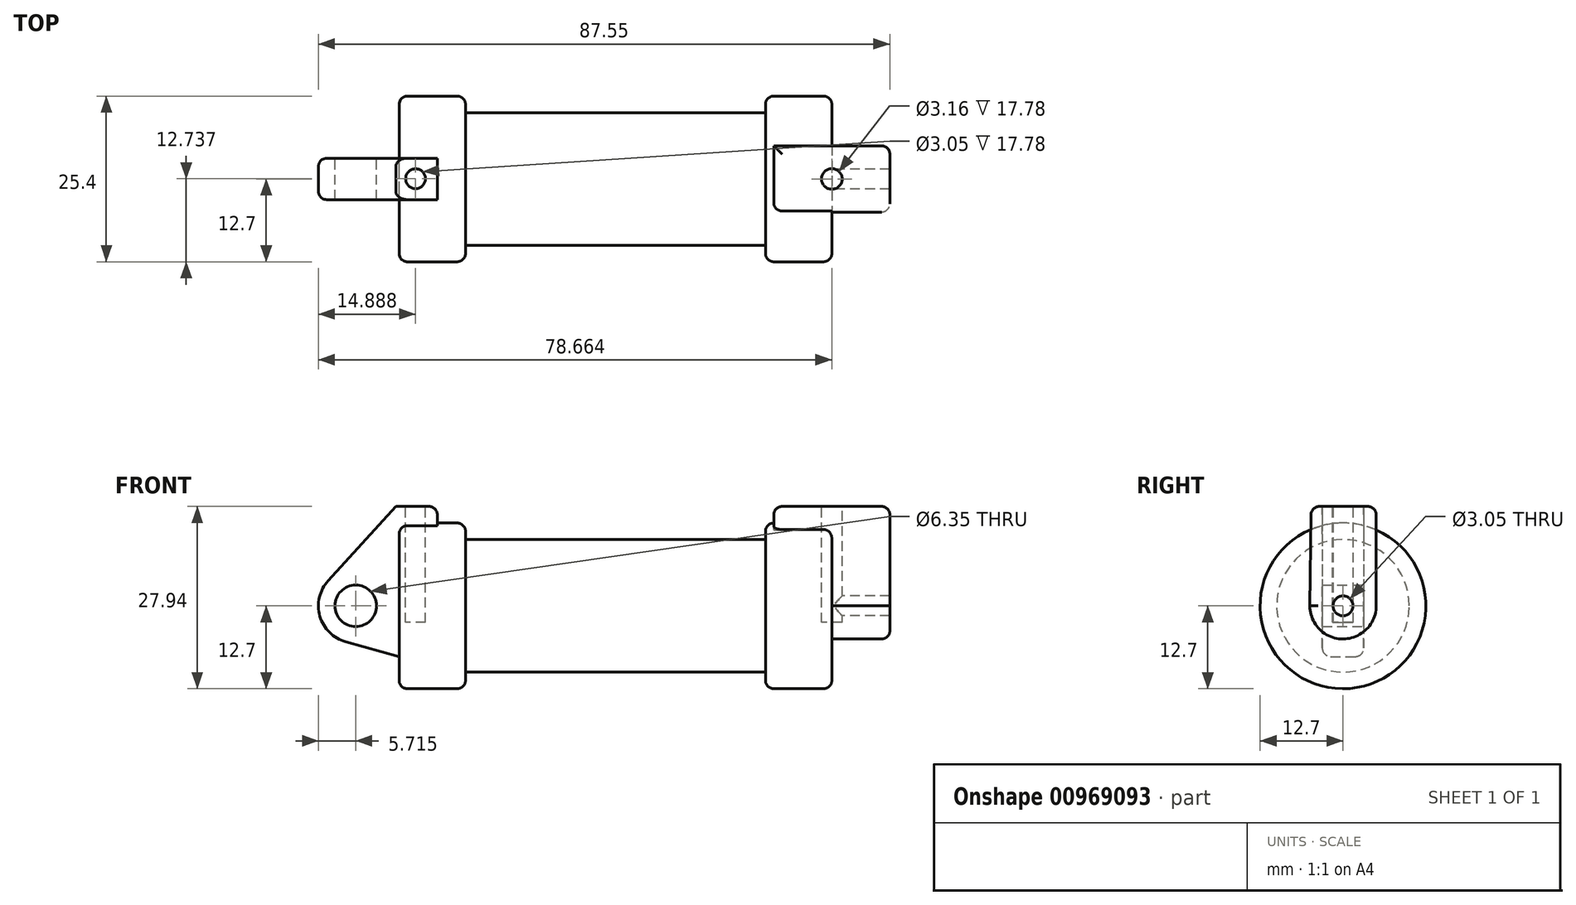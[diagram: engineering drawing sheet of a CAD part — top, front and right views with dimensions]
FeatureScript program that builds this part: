
annotation { "Feature Type Name" : "Feature", "Feature Type Description" : "" }
export const myFeature = defineFeature(function(context is Context, id is Id, definition is map)
    precondition{}
    {
        {
            var Q0;
            Q0=qCreatedBy(makeId("Front.planeOp"),FACE);
            var sketch = newSketch(context, id + "F0", { "sketchPlane" : qUnion([Q0])});
            skLineSegment(sketch, "E0", {"start": v(0, 0) * mm, "end": v(0, 12.7) * mm});
            skLineSegment(sketch, "E1", {"start": v(0, 12.7) * mm, "end": v(10.16, 12.7) * mm});
            skLineSegment(sketch, "E2", {"start": v(10.16, 12.7) * mm, "end": v(10.16, 10.16) * mm});
            skLineSegment(sketch, "E3", {"start": v(10.16, 10.16) * mm, "end": v(56.13, 10.16) * mm});
            skLineSegment(sketch, "E4", {"start": v(56.13, 10.16) * mm, "end": v(56.13, 12.7) * mm});
            skLineSegment(sketch, "E5", {"start": v(56.13, 12.7) * mm, "end": v(66.3, 12.7) * mm});
            skLineSegment(sketch, "E6", {"start": v(66.3, 12.7) * mm, "end": v(66.3, 0) * mm});
            skLineSegment(sketch, "E7", {"start": v(66.3, 0) * mm, "end": v(0, 0) * mm});
            skLineSegment(sketch, "E8", {"start": v(5.84, 15.24) * mm, "end": v(-0.5, 15.24) * mm});
            skLineSegment(sketch, "E9", {"start": v(-0.5, 15.24) * mm, "end": v(-10.88, 3.85) * mm});
            skLineSegment(sketch, "E10", {"start": v(0, 0) * mm, "end": v(-6.65, 0) * mm});
            skCircle(sketch, "E11", {"center": v(-6.65, 0) * mm, "radius": 5.72 * mm});
            skCircle(sketch, "E12", {"center": v(-6.65, 0) * mm, "radius": 3.18 * mm});
            skLineSegment(sketch, "E13", {"start": v(5.84, 15.24) * mm, "end": v(5.84, -9.4) * mm});
            skLineSegment(sketch, "E14", {"start": v(5.84, -9.4) * mm, "end": v(-8.18, -5.5) * mm});
            skSolve(sketch);
        }
        {
            var Q0;
            {var subQ0=sQuery(id+"F0.wireOp",EDGE,"E2");Q0=makeQuery(id+"F0.imprint","IMPRINT",FACE,{"disambiguationData":[TD([[makeQuery(id+"F0.imprint","IMPRINT",EDGE,{"derivedFrom":subQ0}),-1.0]])]});}
            var Q1;
            {var subQ0=sQuery(id+"F0.wireOp",EDGE,"E0");Q1=makeQuery(id+"F0.imprint","IMPRINT",FACE,{"disambiguationData":[TD([[makeQuery(id+"F0.imprint","IMPRINT",EDGE,{"derivedFrom":subQ0}),-1.0]])]});}
            var Q2;
            Q2=sQuery(id+"F0.wireOp",EDGE,"E7");
            revolve(context, id + "F1", {"surfaceOperationType" : NewSurfaceOperationType.NEW, "entities" : qUnion([Q0, Q1]), "axis" : qUnion([Q2]), "revolveType" : RevolveType.FULL});
        }
        {
            var Q0;
            {var subQ1=sQuery(id+"F0.wireOp",EDGE,"E0");Q0=makeQuery(id+"F0.imprint","IMPRINT",FACE,{"disambiguationData":[TD([[makeQuery(id+"F0.imprint","IMPRINT",EDGE,{"derivedFrom":subQ1}),1.0]])]});}
            var Q1;
            {var subQ5=sQuery(id+"F0.wireOp",EDGE,"E12");Q1=makeQuery(id+"F0.imprint","IMPRINT",FACE,{"disambiguationData":[TD([[makeQuery(id+"F0.imprint","IMPRINT",EDGE,{"derivedFrom":subQ5}),-1.0]])]});}
            var Q2;
            {var subQ0=sQuery(id+"F0.wireOp",EDGE,"E0");Q2=makeQuery(id+"F0.imprint","IMPRINT",FACE,{"disambiguationData":[TD([[makeQuery(id+"F0.imprint","IMPRINT",EDGE,{"derivedFrom":subQ0}),-1.0]])]});}
            var Q3;
            {var subQ0=sQuery(id+"F0.wireOp",EDGE,"E14");Q3=makeQuery(id+"F0.imprint","IMPRINT",FACE,{"disambiguationData":[TD([[makeQuery(id+"F0.imprint","IMPRINT",EDGE,{"derivedFrom":subQ0}),-1.0]])]});}
            extrude(context, id + "F2", {"entities" : qUnion([Q0, Q1, Q2, Q3]), "operationType" : NewBodyOperationType.ADD, "depth" : 6.35 * mm, "offsetDistance" : 25.4 * mm, "symmetric" : true});
        }
        {
            var Q0;
            Q0=makeQuery(id+"F1.opRevolve","SWEPT_FACE",FACE,{"disambiguationData":[OSD([sQuery(id+"F0.wireOp",EDGE,"E6")])]});
            var sketch = newSketch(context, id + "F3", { "sketchPlane" : qUnion([Q0])});
            skCircle(sketch, "E15", {"center": v(0, 0) * mm, "radius": 5.08 * mm});
            skCircle(sketch, "E16", {"center": v(0, 0) * mm, "radius": 1.52 * mm});
            skLineSegment(sketch, "E17", {"start": v(5.08, 0.02) * mm, "end": v(5.08, 15.24) * mm});
            skLineSegment(sketch, "E18", {"start": v(5.08, 15.24) * mm, "end": v(-4.88, 15.24) * mm});
            skLineSegment(sketch, "E19", {"start": v(-4.88, 15.24) * mm, "end": v(-5.08, 0) * mm});
            skSolve(sketch);
        }
        {
            var Q0;
            {var subQ0=sQuery(id+"F3.wireOp",EDGE,"E18");Q0=makeQuery(id+"F3.imprint","IMPRINT",FACE,{"disambiguationData":[TD([[makeQuery(id+"F3.imprint","IMPRINT",EDGE,{"derivedFrom":subQ0}),1.0]])]});}
            var Q1;
            {var subQ0=sQuery(id+"F3.wireOp",EDGE,"E17");var subQ1=sQuery(id+"F3.wireOp",EDGE,"E15");var subQ2=makeQuery(id+"F3.imprint","INTERSECT",VERTEX,{"derivedFrom":[subQ1,subQ0]});Q1=makeQuery(id+"F3.imprint","IMPRINT",FACE,{"disambiguationData":[TD([[makeQuery(id+"F3.imprint","IMPRINT",EDGE,{"disambiguationData":[TD([[subQ2,-1.0]])],"derivedFrom":subQ1}),-1.0]])]});}
            var Q2;
            Q2=makeQuery(id+"F3.imprint","IMPRINT",FACE,{"disambiguationData":[TD([[makeQuery(id+"F3.imprint","IMPRINT",EDGE,{"derivedFrom":sQuery(id+"F3.wireOp",EDGE,"E16")}),-1.0]])]});
            extrude(context, id + "F4", {"entities" : qUnion([Q0, Q1, Q2]), "operationType" : NewBodyOperationType.ADD, "depth" : 17.78 * mm, "offsetDistance" : 25.4 * mm, "symmetric" : true});
        }
        {
            var Q0;
            Q0=makeQuery(id+"F4.opExtrude","SWEPT_FACE",FACE,{"disambiguationData":[OSD([sQuery(id+"F3.wireOp",EDGE,"E18")])]});
            var sketch = newSketch(context, id + "F5", { "sketchPlane" : qUnion([Q0])});
            skCircle(sketch, "E20", {"center": v(66.3, 0) * mm, "radius": 1.58 * mm});
            skSolve(sketch);
        }
        {
            var Q0;
            Q0 = qSketchRegion(id + "F5", true);
            extrude(context, id + "F6", {"entities" : qUnion([Q0]), "operationType" : NewBodyOperationType.REMOVE, "oppositeDirection" : true, "depth" : 17.78 * mm, "offsetDistance" : 25.4 * mm});
        }
        {
            var Q0;
            Q0=makeQuery(id+"F2.opExtrude","SWEPT_FACE",FACE,{"disambiguationData":[OSD([sQuery(id+"F0.wireOp",EDGE,"E8")])]});
            var sketch = newSketch(context, id + "F7", { "sketchPlane" : qUnion([Q0])});
            skCircle(sketch, "E21", {"center": v(2.52, 0.04) * mm, "radius": 1.52 * mm});
            skSolve(sketch);
        }
        {
            var Q0;
            Q0 = qSketchRegion(id + "F7", true);
            extrude(context, id + "F8", {"entities" : qUnion([Q0]), "operationType" : NewBodyOperationType.REMOVE, "oppositeDirection" : true, "depth" : 17.78 * mm, "offsetDistance" : 25.4 * mm});
        }
        {
            var Q0;
            Q0=makeQuery(id+"F2.opExtrude","CAP_EDGE",EDGE,{"disambiguationData":[OSD([sQuery(id+"F0.wireOp",EDGE,"E9")])],"isStart":false});
            var Q1;
            Q1=makeQuery(id+"F2.opExtrude","CAP_EDGE",EDGE,{"disambiguationData":[OSD([sQuery(id+"F0.wireOp",EDGE,"E9")])],"isStart":true});
            fillet(context, id + "F9", {"entities" : qUnion([Q0, Q1]), "radius" : 1.27 * mm, "tangentPropagation" : true, "allowEdgeOverflow" : false});
        }
        {
            var Q0;
            Q0=makeQuery(id+"F1.opRevolve","SWEPT_EDGE",EDGE,{"disambiguationData":[OSD([sQuery(id+"F0.wireOp",EDGE,"E0"),sQuery(id+"F0.wireOp",EDGE,"E1")])]});
            var Q1;
            Q1=makeQuery(id+"F1.opRevolve","SWEPT_EDGE",EDGE,{"disambiguationData":[OSD([sQuery(id+"F0.wireOp",EDGE,"E1"),sQuery(id+"F0.wireOp",EDGE,"E2")])]});
            var Q2;
            Q2=makeQuery(id+"F1.opRevolve","SWEPT_EDGE",EDGE,{"disambiguationData":[OSD([sQuery(id+"F0.wireOp",EDGE,"E4"),sQuery(id+"F0.wireOp",EDGE,"E5")])]});
            var Q3;
            Q3=makeQuery(id+"F1.opRevolve","SWEPT_EDGE",EDGE,{"disambiguationData":[OSD([sQuery(id+"F0.wireOp",EDGE,"E5"),sQuery(id+"F0.wireOp",EDGE,"E6")])]});
            var Q4;
            Q4=makeQuery(id+"F4.opExtrude","CAP_EDGE",EDGE,{"disambiguationData":[OSD([sQuery(id+"F3.wireOp",EDGE,"E19")])],"isStart":false});
            var Q5;
            Q5=makeQuery(id+"F4.opExtrude","CAP_EDGE",EDGE,{"disambiguationData":[OSD([sQuery(id+"F3.wireOp",EDGE,"E17")])],"isStart":false});
            var Q6;
            Q6=makeQuery(id+"F4.opExtrude","CAP_EDGE",EDGE,{"disambiguationData":[OSD([sQuery(id+"F3.wireOp",EDGE,"E18")])],"isStart":false});
            var Q7;
            Q7=makeQuery(id+"F4.opExtrude","CAP_EDGE",EDGE,{"disambiguationData":[OSD([sQuery(id+"F3.wireOp",EDGE,"E15")])],"isStart":false});
            var Q8;
            Q8=makeQuery(id+"F4.opExtrude","SWEPT_EDGE",EDGE,{"disambiguationData":[OSD([sQuery(id+"F3.wireOp",EDGE,"E18"),sQuery(id+"F3.wireOp",EDGE,"E19")])]});
            var Q9;
            Q9=makeQuery(id+"F4.opExtrude","CAP_EDGE",EDGE,{"disambiguationData":[OSD([sQuery(id+"F3.wireOp",EDGE,"E19")])],"isStart":true});
            var Q10;
            Q10=makeQuery(id+"F4.opExtrude","SWEPT_EDGE",EDGE,{"disambiguationData":[OSD([sQuery(id+"F3.wireOp",EDGE,"E17"),sQuery(id+"F3.wireOp",EDGE,"E18")])]});
            var Q11;
            Q11=makeQuery(id+"F4.opExtrude","CAP_EDGE",EDGE,{"disambiguationData":[OSD([sQuery(id+"F3.wireOp",EDGE,"E18")])],"isStart":true});
            var Q12;
            Q12=makeQuery(id+"F2.opExtrude","SWEPT_EDGE",EDGE,{"disambiguationData":[OSD([sQuery(id+"F0.wireOp",EDGE,"E8"),sQuery(id+"F0.wireOp",EDGE,"E13")])]});
            fillet(context, id + "F10", {"entities" : qUnion([Q0, Q1, Q2, Q3, Q4, Q5, Q6, Q7, Q8, Q9, Q10, Q11, Q12]), "radius" : 1.27 * mm, "tangentPropagation" : true, "allowEdgeOverflow" : false});
        }
    });
